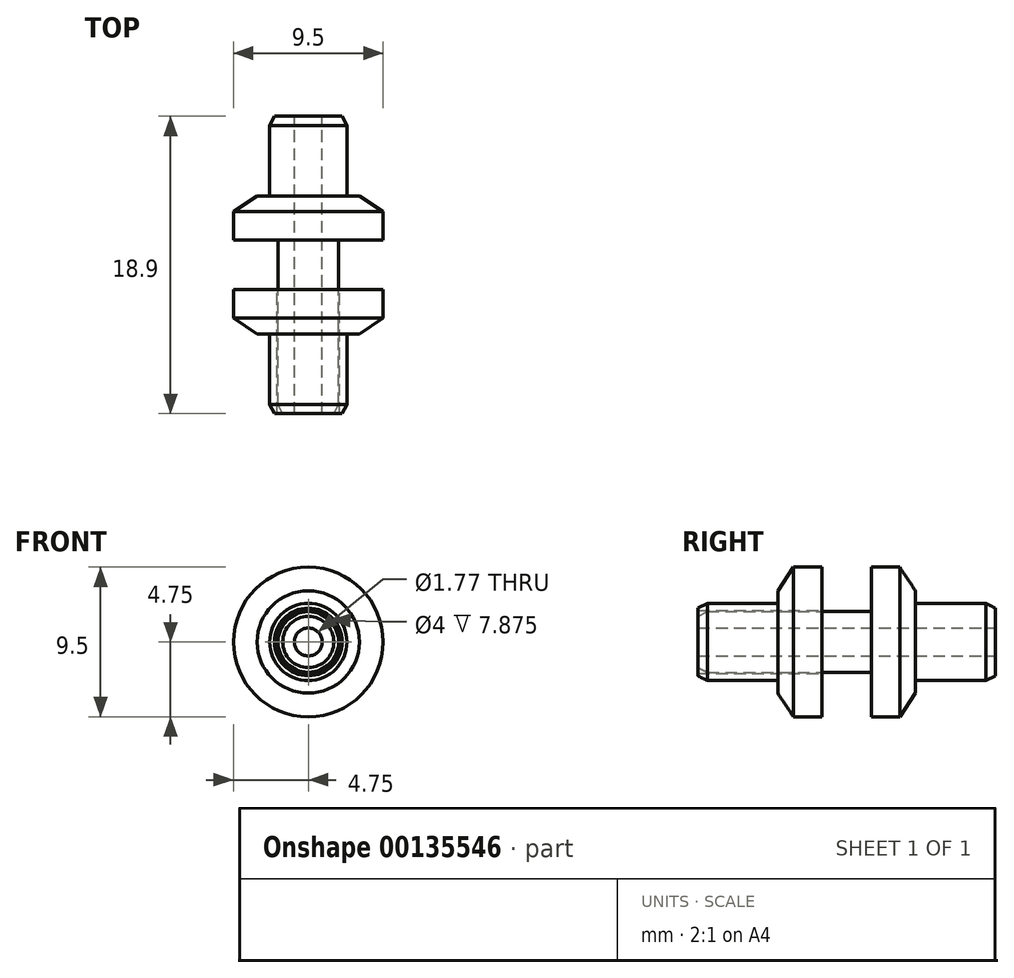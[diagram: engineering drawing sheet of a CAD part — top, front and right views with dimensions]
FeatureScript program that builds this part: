
annotation { "Feature Type Name" : "Feature", "Feature Type Description" : "" }
export const myFeature = defineFeature(function(context is Context, id is Id, definition is map)
    precondition{}
    {
        {
            var Q0;
            Q0=qCreatedBy(makeId("Right.planeOp"),FACE);
            var sketch = newSketch(context, id + "F0", { "sketchPlane" : qUnion([Q0])});
            skLineSegment(sketch, "E0", {"start": v(0, 0) * mm, "end": v(-18.9, 0) * mm, "construction": true});
            skLineSegment(sketch, "E1", {"start": v(0, 0.8) * mm, "end": v(-18.9, 0.8) * mm, "construction": true});
            skLineSegment(sketch, "E2", {"start": v(0, 2.5) * mm, "end": v(-5, 2.5) * mm, "construction": true});
            skLineSegment(sketch, "E3", {"start": v(-7.95, 2) * mm, "end": v(-10.95, 2) * mm, "construction": true});
            skLineSegment(sketch, "E4", {"start": v(-18.9, 2.5) * mm, "end": v(-13.9, 2.5) * mm, "construction": true});
            skLineSegment(sketch, "E5", {"start": v(-18.9, 0) * mm, "end": v(-18.9, 2.5) * mm, "construction": true});
            skLineSegment(sketch, "E6", {"start": v(-7.95, 2) * mm, "end": v(-7.95, 2.5) * mm, "construction": true});
            skLineSegment(sketch, "E7", {"start": v(-7.95, 2.5) * mm, "end": v(-5, 2.5) * mm, "construction": true});
            skLineSegment(sketch, "E8", {"start": v(-10.95, 2) * mm, "end": v(-10.95, 2.5) * mm, "construction": true});
            skLineSegment(sketch, "E9", {"start": v(-10.95, 2.5) * mm, "end": v(-13.9, 2.5) * mm, "construction": true});
            skLineSegment(sketch, "E10", {"start": v(-18.9, 2.5) * mm, "end": v(-18.9, 8.18) * mm});
            skLineSegment(sketch, "E11", {"start": v(-18.9, 8.18) * mm, "end": v(-13.9, 8.18) * mm});
            skLineSegment(sketch, "E12", {"start": v(-13.9, 8.18) * mm, "end": v(-13.9, 2.5) * mm});
            skLineSegment(sketch, "E13", {"start": v(-10.95, 2.5) * mm, "end": v(-10.95, 8.18) * mm});
            skLineSegment(sketch, "E14", {"start": v(-10.95, 8.18) * mm, "end": v(-7.95, 8.18) * mm});
            skLineSegment(sketch, "E15", {"start": v(-7.95, 8.18) * mm, "end": v(-7.95, 2.5) * mm});
            skLineSegment(sketch, "E16", {"start": v(-5, 2.5) * mm, "end": v(-5, 8.18) * mm});
            skLineSegment(sketch, "E17", {"start": v(-5, 8.18) * mm, "end": v(0, 8.18) * mm});
            skLineSegment(sketch, "E18", {"start": v(0, 8.18) * mm, "end": v(0, 2.5) * mm});
            skLineSegment(sketch, "E19", {"start": v(-18.9, 0.88) * mm, "end": v(0, 0.89) * mm});
            skLineSegment(sketch, "E20", {"start": v(0, 0.88) * mm, "end": v(0, 2.45) * mm});
            skLineSegment(sketch, "E21", {"start": v(0, 2.45) * mm, "end": v(-5.07, 2.45) * mm});
            skLineSegment(sketch, "E22", {"start": v(-5.07, 2.45) * mm, "end": v(-5.07, 4.75) * mm});
            skLineSegment(sketch, "E23", {"start": v(-5.08, 4.75) * mm, "end": v(-7.88, 4.75) * mm});
            skLineSegment(sketch, "E24", {"start": v(-7.88, 4.75) * mm, "end": v(-7.88, 1.93) * mm});
            skLineSegment(sketch, "E25", {"start": v(-7.88, 1.93) * mm, "end": v(-18.9, 1.92) * mm});
            skLineSegment(sketch, "E26", {"start": v(-18.9, 1.93) * mm, "end": v(-18.9, 0.88) * mm});
            skLineSegment(sketch, "E27", {"start": v(-18.9, 2) * mm, "end": v(-11.03, 2) * mm});
            skLineSegment(sketch, "E28", {"start": v(-11.03, 2) * mm, "end": v(-11.03, 4.75) * mm});
            skLineSegment(sketch, "E29", {"start": v(-11.03, 4.75) * mm, "end": v(-13.83, 4.75) * mm});
            skLineSegment(sketch, "E30", {"start": v(-13.83, 4.75) * mm, "end": v(-13.83, 2.45) * mm});
            skLineSegment(sketch, "E31", {"start": v(-13.83, 2.45) * mm, "end": v(-18.9, 2.45) * mm});
            skLineSegment(sketch, "E32", {"start": v(-18.9, 2.45) * mm, "end": v(-18.9, 2) * mm});
            skLineSegment(sketch, "E33", {"start": v(-9.45, 2) * mm, "end": v(-9.45, 8.18) * mm, "construction": true});
            skSolve(sketch);
        }
        {
            var Q0;
            Q0 = qSketchRegion(id + "F0", true);
            var Q1;
            Q1=sQuery(id+"F0.wireOp",EDGE,"E0");
            revolve(context, id + "F1", {"entities" : qUnion([Q0]), "axis" : qUnion([Q1]), "revolveType" : RevolveType.FULL});
        }
        {
            var Q0;
            Q0=makeQuery(id+"F1.opRevolve","SWEPT_EDGE",EDGE,{"disambiguationData":[OSD([sQuery(id+"F0.wireOp",EDGE,"E31"),sQuery(id+"F0.wireOp",EDGE,"E32")])]});
            var Q1;
            Q1=makeQuery(id+"F1.opRevolve","SWEPT_EDGE",EDGE,{"disambiguationData":[OSD([sQuery(id+"F0.wireOp",EDGE,"E25"),sQuery(id+"F0.wireOp",EDGE,"E26")])]});
            chamfer(context, id + "F2", {"entities" : qUnion([Q0, Q1]), "chamferType" : ChamferType.TWO_OFFSETS, "width1" : 0.6 * mm, "oppositeDirection" : false, "width2" : 0.3 * mm, "tangentPropagation" : true});
        }
        {
            var Q0;
            Q0=makeQuery(id+"F1.opRevolve","SWEPT_EDGE",EDGE,{"disambiguationData":[OSD([sQuery(id+"F0.wireOp",EDGE,"E20"),sQuery(id+"F0.wireOp",EDGE,"E21")])]});
            chamfer(context, id + "F3", {"entities" : qUnion([Q0]), "chamferType" : ChamferType.TWO_OFFSETS, "width1" : 0.3 * mm, "oppositeDirection" : false, "width2" : 0.6 * mm, "tangentPropagation" : true});
        }
        {
            var Q0;
            Q0=makeQuery(id+"F1.opRevolve","SWEPT_EDGE",EDGE,{"disambiguationData":[OSD([sQuery(id+"F0.wireOp",EDGE,"E29"),sQuery(id+"F0.wireOp",EDGE,"E30")])]});
            chamfer(context, id + "F4", {"entities" : qUnion([Q0]), "chamferType" : ChamferType.TWO_OFFSETS, "width1" : 1 * mm, "oppositeDirection" : false, "width2" : 1.5 * mm, "tangentPropagation" : true});
        }
        {
            var Q0;
            Q0=makeQuery(id+"F1.opRevolve","SWEPT_EDGE",EDGE,{"disambiguationData":[OSD([sQuery(id+"F0.wireOp",EDGE,"E22"),sQuery(id+"F0.wireOp",EDGE,"E23")])]});
            chamfer(context, id + "F5", {"entities" : qUnion([Q0]), "chamferType" : ChamferType.TWO_OFFSETS, "width1" : 1.5 * mm, "oppositeDirection" : false, "width2" : 1 * mm, "tangentPropagation" : true});
        }
    });
